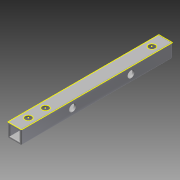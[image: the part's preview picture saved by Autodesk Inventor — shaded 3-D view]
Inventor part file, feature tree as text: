
AUTODESK INVENTOR PART (.ipt)
format: ipt  version: 2013 (Build 170138000, 138)  size: 161,280 bytes
history: native  units: in
note: dims shown in document units (in); Inventor stores cm internally (conversion verified against a paired STEP export)
features: sketch x6, extrude x5, fillet x1
ambient origin geometry x8: Origin, YZ Plane, XZ Plane, XY Plane, X Axis, Y Axis, Z Axis, Center Point
bodies: Solid1 (feature_tree)
feature tree (12):
  extrude  "Extrusion1"  Depth=1.0in
  extrude  "Extrusion2"  Depth=1.0in
  extrude  "Extrusion3"  Depth=1.0in
  extrude  "Extrusion4"  Depth=11.0in TaperAngle=0.0deg
  sketch  "Sketch5"  dims[d10=0.15in d11=0.15in d12=0.15in]
  extrude  "Extrusion5"  Depth=0.15in
  fillet  "Fillet1"  Radius=0.15in
  sketch  "Sketch1"  dims[d0=1.0in d1=1.0in]
  sketch  "Sketch2"  dims[d2=11.0in d3=0.0in d4=1.0in]
  sketch  "Sketch3"  dims[d5=0.5in d6=1.0in]
  sketch  "Sketch4"  dims[d7=0.5in d8=11.0in d9=0.0in]
  sketch  "Sketch6"  dims[d13=0.15in d14=0.15in d15=0.15in d16=0.15in d17=0.15in d18=11.0in d19=0.0in d20=1.0in d21=0.5in d22=11.0in d23=0.0in d24=1.5in d25=0.5in d26=4.0in d27=0.5in d28=11.0in d29=0.0in d30=0.0625in]
